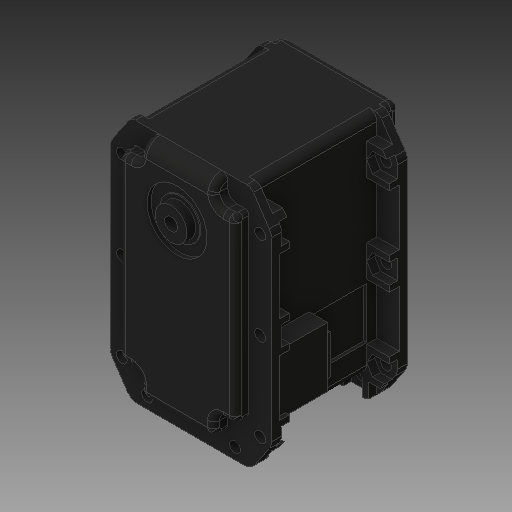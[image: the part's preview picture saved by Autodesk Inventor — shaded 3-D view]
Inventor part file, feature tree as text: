
AUTODESK INVENTOR PART (.ipt)
format: ipt  version: 2019 (Build 230136000, 136)  size: 722,432 bytes
history: native  units: in
note: dims shown in document units (in); Inventor stores cm internally (conversion verified against a paired STEP export)
features: other x3, sketch x3
ambient origin geometry x8: Origin, YZ Plane, XZ Plane, XY Plane, X Axis, Y Axis, Z Axis, Center Point
bodies: Solid1 (feature_tree)
feature tree (6):
  other  "MX-64T.ipt"
  other  "Solid1::MX-64T.ipt"
  other  "TaggingFeature1"
  sketch  "Sketch1"  dims[d0=0.3937in]
  sketch  "Sketch2"  dims[d2=0.1575in d3=0.0in d4=0.0in]
  sketch  "Sketch3"
